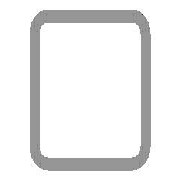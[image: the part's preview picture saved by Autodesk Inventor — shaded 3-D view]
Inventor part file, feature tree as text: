
AUTODESK INVENTOR PART (.ipt)
format: ipt  version: 2022 (Build 260153000, 153)  size: 138,752 bytes
history: native  units: mm (DEFAULTED — no unit token found)
features: other x4, sketch x3, plane x1
ambient origin geometry x8: Origin, YZ Plane, XZ Plane, XY Plane, X Axis, Y Axis, Z Axis, Center Point
bodies: Solid1 (feature_tree), Body (feature_tree)
feature tree (8):
  parser-record x1  (decoder bookkeeping rows leaked as tree rows — omitted from the tree; the rows remain in map.json)
  other  "Driven Length"
  other  "Start plane"
  other  "End plane"
  sketch  "Sketch"  dims[d7=4.5mm d10=30.0mm d11=30.0mm d12=3.0mm d13=-0.0mm d14=180.0mm d15=15.0mm d16=15.0mm d17=90.0deg d18=180.0mm]
  sketch  "Sketch3"  dims[d3=180.0mm]
  plane  "Work Plane3"
  sketch  "Sketch4"  dims[d4=0.0mm]
